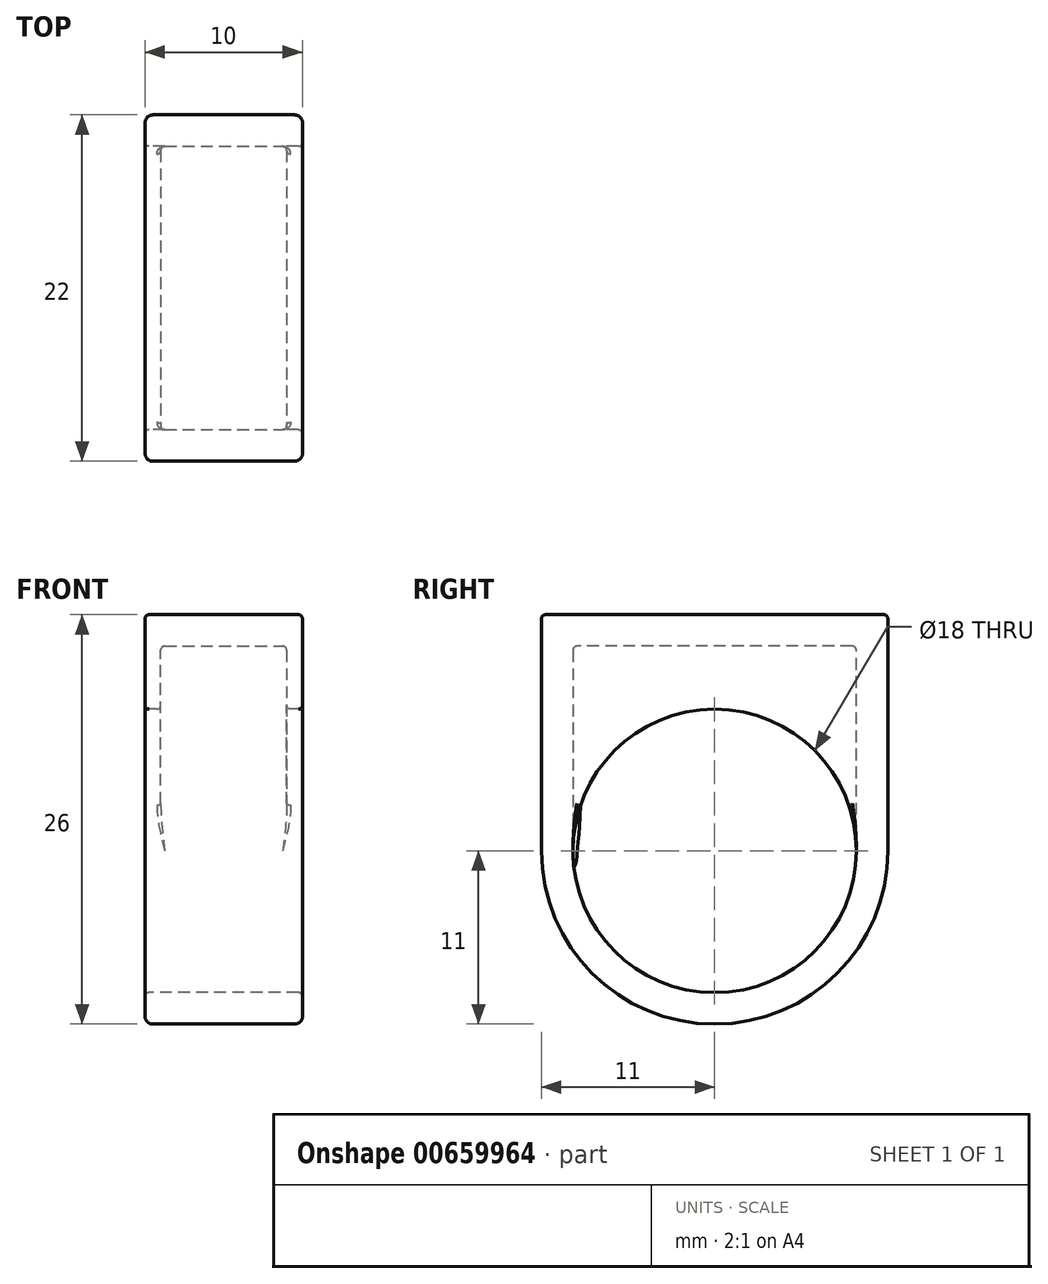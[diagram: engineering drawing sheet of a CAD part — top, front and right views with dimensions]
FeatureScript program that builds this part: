
annotation { "Feature Type Name" : "Feature", "Feature Type Description" : "" }
export const myFeature = defineFeature(function(context is Context, id is Id, definition is map)
    precondition{}
    {
        {
            var Q0;
            Q0=qCreatedBy(makeId("Right.planeOp"),FACE);
            var sketch = newSketch(context, id + "F0", { "sketchPlane" : qUnion([Q0])});
            skCircle(sketch, "E0", {"center": v(0, 0) * mm, "radius": 9 * mm});
            skCircle(sketch, "E1", {"center": v(0, 0) * mm, "radius": 11 * mm});
            skLineSegment(sketch, "E2", {"start": v(-11, 0) * mm, "end": v(-11, 15) * mm});
            skLineSegment(sketch, "E3", {"start": v(11, 0) * mm, "end": v(11, 15) * mm});
            skLineSegment(sketch, "E4", {"start": v(-11, 15) * mm, "end": v(11, 15) * mm});
            skSolve(sketch);
        }
        {
            var Q0;
            Q0=qSketchRegion(id+"F0",true);
            extrude(context, id + "F1", {"entities" : qUnion([Q0]), "endBound" : BoundingType.SYMMETRIC, "depth" : 10 * mm, "offsetDistance" : 25 * mm});
        }
        {
            var Q0;
            Q0=qCreatedBy(makeId("Right.planeOp"),FACE);
            var sketch = newSketch(context, id + "F2", { "sketchPlane" : qUnion([Q0])});
            skLineSegment(sketch, "E5.0", {"start": v(-9, 13) * mm, "end": v(-9, 0) * mm});
            skLineSegment(sketch, "E5.1", {"start": v(9, 13) * mm, "end": v(-9, 13) * mm});
            skLineSegment(sketch, "E5.2", {"start": v(9, 0) * mm, "end": v(9, 13) * mm});
            skArc(sketch, "E5.3", {"start": v(-9, 0) * mm, "mid": v(0, -9) * mm, "end": v(9, 0) * mm});
            skSolve(sketch);
        }
        {
            var Q0;
            Q0 = qSketchRegion(id + "F2", true);
            extrude(context, id + "F3", {"entities" : qUnion([Q0]), "operationType" : NewBodyOperationType.REMOVE, "endBound" : BoundingType.SYMMETRIC, "oppositeDirection" : true, "depth" : 8 * mm, "offsetDistance" : 25 * mm});
        }
        {
            var Q0;
            Q0=makeQuery(id+"F1.opExtrude","CAP_EDGE",EDGE,{"disambiguationData":[OSD([sQuery(id+"F0.wireOp",EDGE,"E2")])],"isStart":false});
            var Q1;
            Q1=makeQuery(id+"F1.opExtrude","CAP_EDGE",EDGE,{"disambiguationData":[OSD([sQuery(id+"F0.wireOp",EDGE,"E2")])],"isStart":true});
            fillet(context, id + "F4", {"entities" : qUnion([Q0, Q1]), "radius" : 0.5 * mm, "tangentPropagation" : true, "allowEdgeOverflow" : false});
        }
        {
            var Q0;
            {var subQ0=sQuery(id+"F0.wireOp",EDGE,"E2");Q0=makeQuery(id+"F4.opFillet","BLEND_EDGE",EDGE,{"blendedFrom":[makeQuery(id+"F1.opExtrude","CAP_EDGE",EDGE,{"disambiguationData":[OSD([subQ0])],"isStart":true}),makeQuery(id+"F1.opExtrude","SWEPT_FACE",FACE,{"disambiguationData":[OSD([subQ0])]})],"blendedInto":[makeQuery(id+"F1.opExtrude","SWEPT_FACE",FACE,{"disambiguationData":[OSD([subQ0])]})]});}
            var Q1;
            {var subQ0=sQuery(id+"F0.wireOp",EDGE,"E2");Q1=makeQuery(id+"F4.opFillet","BLEND_EDGE",EDGE,{"blendedFrom":[makeQuery(id+"F1.opExtrude","CAP_EDGE",EDGE,{"disambiguationData":[OSD([subQ0])],"isStart":false}),makeQuery(id+"F1.opExtrude","SWEPT_FACE",FACE,{"disambiguationData":[OSD([subQ0])]})],"blendedInto":[makeQuery(id+"F1.opExtrude","SWEPT_FACE",FACE,{"disambiguationData":[OSD([subQ0])]})]});}
            var Q2;
            Q2=makeQuery(id+"F1.opExtrude","CAP_EDGE",EDGE,{"disambiguationData":[OSD([sQuery(id+"F0.wireOp",EDGE,"E0")])],"isStart":false});
            var Q3;
            Q3=makeQuery(id+"F4.opFillet","BLEND_EDGE",EDGE,{"blendedFrom":[makeQuery(id+"F1.opExtrude","CAP_EDGE",EDGE,{"disambiguationData":[OSD([sQuery(id+"F0.wireOp",EDGE,"E1")])],"isStart":false}),makeQuery(id+"F1.opExtrude","CAP_EDGE",EDGE,{"disambiguationData":[OSD([sQuery(id+"F0.wireOp",EDGE,"E3")])],"isStart":false})],"blendedInto":[]});
            var Q4;
            Q4=makeQuery(id+"F1.opExtrude","SWEPT_EDGE",EDGE,{"disambiguationData":[OSD([sQuery(id+"F0.wireOp",EDGE,"E3"),sQuery(id+"F0.wireOp",EDGE,"E4")])]});
            var Q5;
            Q5=makeQuery(id+"F1.opExtrude","SWEPT_EDGE",EDGE,{"disambiguationData":[OSD([sQuery(id+"F0.wireOp",EDGE,"E1"),sQuery(id+"F0.wireOp",EDGE,"E3")])]});
            var Q6;
            {var subQ0=sQuery(id+"F0.wireOp",EDGE,"E2");Q6=makeQuery(id+"F4.opFillet","BLEND_EDGE",EDGE,{"blendedFrom":[makeQuery(id+"F1.opExtrude","CAP_EDGE",EDGE,{"disambiguationData":[OSD([subQ0])],"isStart":false}),makeQuery(id+"F1.opExtrude","CAP_FACE",FACE,{"disambiguationData":[OSD([sQuery(id+"F0.wireOp",EDGE,"E0"),sQuery(id+"F0.wireOp",EDGE,"E1"),subQ0,sQuery(id+"F0.wireOp",EDGE,"E3"),sQuery(id+"F0.wireOp",EDGE,"E4")])],"isStart":false})],"blendedInto":[makeQuery(id+"F1.opExtrude","CAP_FACE",FACE,{"disambiguationData":[OSD([sQuery(id+"F0.wireOp",EDGE,"E0"),sQuery(id+"F0.wireOp",EDGE,"E1"),subQ0,sQuery(id+"F0.wireOp",EDGE,"E3"),sQuery(id+"F0.wireOp",EDGE,"E4")])],"isStart":false})]});}
            var Q7;
            Q7=makeQuery(id+"F4.opFillet","BLEND_EDGE",EDGE,{"blendedFrom":[makeQuery(id+"F1.opExtrude","CAP_EDGE",EDGE,{"disambiguationData":[OSD([sQuery(id+"F0.wireOp",EDGE,"E3")])],"isStart":false}),makeQuery(id+"F1.opExtrude","SWEPT_FACE",FACE,{"disambiguationData":[OSD([sQuery(id+"F0.wireOp",EDGE,"E4")])]})],"blendedInto":[makeQuery(id+"F1.opExtrude","SWEPT_FACE",FACE,{"disambiguationData":[OSD([sQuery(id+"F0.wireOp",EDGE,"E4")])]})]});
            var Q8;
            Q8=makeQuery(id+"F3.boolean.opBoolean","INTERSECT",EDGE,{"derivedFrom":[makeQuery(id+"F1.opExtrude","SWEPT_FACE",FACE,{"disambiguationData":[OSD([sQuery(id+"F0.wireOp",EDGE,"E0")])]}),makeQuery(id+"F3.opExtrude","CAP_FACE",FACE,{"disambiguationData":[OSD([sQuery(id+"F2.wireOp",EDGE,"E5.0"),sQuery(id+"F2.wireOp",EDGE,"E5.1"),sQuery(id+"F2.wireOp",EDGE,"E5.2"),sQuery(id+"F2.wireOp",EDGE,"E5.3")])],"isStart":false})]});
            var Q9;
            Q9=makeQuery(id+"F3.boolean.opBoolean","INTERSECT",EDGE,{"derivedFrom":[makeQuery(id+"F1.opExtrude","SWEPT_FACE",FACE,{"disambiguationData":[OSD([sQuery(id+"F0.wireOp",EDGE,"E0")])]}),makeQuery(id+"F3.opExtrude","CAP_FACE",FACE,{"disambiguationData":[OSD([sQuery(id+"F2.wireOp",EDGE,"E5.0"),sQuery(id+"F2.wireOp",EDGE,"E5.1"),sQuery(id+"F2.wireOp",EDGE,"E5.2"),sQuery(id+"F2.wireOp",EDGE,"E5.3")])],"isStart":true})]});
            var Q10;
            Q10=makeQuery(id+"F1.opExtrude","CAP_EDGE",EDGE,{"disambiguationData":[OSD([sQuery(id+"F0.wireOp",EDGE,"E0")])],"isStart":true});
            var Q11;
            {var subQ0=sQuery(id+"F0.wireOp",EDGE,"E1");Q11=makeQuery(id+"F4.opFillet","BLEND_EDGE",EDGE,{"blendedFrom":[makeQuery(id+"F1.opExtrude","CAP_EDGE",EDGE,{"disambiguationData":[OSD([subQ0])],"isStart":true}),makeQuery(id+"F1.opExtrude","SWEPT_FACE",FACE,{"disambiguationData":[OSD([subQ0])]})],"blendedInto":[makeQuery(id+"F1.opExtrude","SWEPT_FACE",FACE,{"disambiguationData":[OSD([subQ0])]})]});}
            var Q12;
            {var subQ0=sQuery(id+"F0.wireOp",EDGE,"E3");Q12=makeQuery(id+"F4.opFillet","BLEND_EDGE",EDGE,{"blendedFrom":[makeQuery(id+"F1.opExtrude","CAP_EDGE",EDGE,{"disambiguationData":[OSD([subQ0])],"isStart":false}),makeQuery(id+"F1.opExtrude","SWEPT_FACE",FACE,{"disambiguationData":[OSD([subQ0])]})],"blendedInto":[makeQuery(id+"F1.opExtrude","SWEPT_FACE",FACE,{"disambiguationData":[OSD([subQ0])]})]});}
            var Q13;
            {var subQ0=sQuery(id+"F0.wireOp",EDGE,"E2");Q13=makeQuery(id+"F4.opFillet","BLEND_EDGE",EDGE,{"blendedFrom":[makeQuery(id+"F1.opExtrude","CAP_EDGE",EDGE,{"disambiguationData":[OSD([subQ0])],"isStart":true}),makeQuery(id+"F1.opExtrude","CAP_FACE",FACE,{"disambiguationData":[OSD([sQuery(id+"F0.wireOp",EDGE,"E0"),sQuery(id+"F0.wireOp",EDGE,"E1"),subQ0,sQuery(id+"F0.wireOp",EDGE,"E3"),sQuery(id+"F0.wireOp",EDGE,"E4")])],"isStart":true})],"blendedInto":[makeQuery(id+"F1.opExtrude","CAP_FACE",FACE,{"disambiguationData":[OSD([sQuery(id+"F0.wireOp",EDGE,"E0"),sQuery(id+"F0.wireOp",EDGE,"E1"),subQ0,sQuery(id+"F0.wireOp",EDGE,"E3"),sQuery(id+"F0.wireOp",EDGE,"E4")])],"isStart":true})]});}
            var Q14;
            {var subQ0=sQuery(id+"F0.wireOp",EDGE,"E1");Q14=makeQuery(id+"F4.opFillet","BLEND_EDGE",EDGE,{"blendedFrom":[makeQuery(id+"F1.opExtrude","CAP_EDGE",EDGE,{"disambiguationData":[OSD([subQ0])],"isStart":false}),makeQuery(id+"F1.opExtrude","SWEPT_FACE",FACE,{"disambiguationData":[OSD([subQ0])]})],"blendedInto":[makeQuery(id+"F1.opExtrude","SWEPT_FACE",FACE,{"disambiguationData":[OSD([subQ0])]})]});}
            var Q15;
            {var subQ0=sQuery(id+"F0.wireOp",EDGE,"E1");Q15=makeQuery(id+"F4.opFillet","BLEND_EDGE",EDGE,{"blendedFrom":[makeQuery(id+"F1.opExtrude","CAP_EDGE",EDGE,{"disambiguationData":[OSD([subQ0])],"isStart":false}),makeQuery(id+"F1.opExtrude","CAP_FACE",FACE,{"disambiguationData":[OSD([sQuery(id+"F0.wireOp",EDGE,"E0"),subQ0,sQuery(id+"F0.wireOp",EDGE,"E2"),sQuery(id+"F0.wireOp",EDGE,"E3"),sQuery(id+"F0.wireOp",EDGE,"E4")])],"isStart":false})],"blendedInto":[makeQuery(id+"F1.opExtrude","CAP_FACE",FACE,{"disambiguationData":[OSD([sQuery(id+"F0.wireOp",EDGE,"E0"),subQ0,sQuery(id+"F0.wireOp",EDGE,"E2"),sQuery(id+"F0.wireOp",EDGE,"E3"),sQuery(id+"F0.wireOp",EDGE,"E4")])],"isStart":false})]});}
            var Q16;
            {var subQ0=sQuery(id+"F0.wireOp",EDGE,"E1");Q16=makeQuery(id+"F4.opFillet","BLEND_EDGE",EDGE,{"blendedFrom":[makeQuery(id+"F1.opExtrude","CAP_EDGE",EDGE,{"disambiguationData":[OSD([subQ0])],"isStart":true}),makeQuery(id+"F1.opExtrude","CAP_FACE",FACE,{"disambiguationData":[OSD([sQuery(id+"F0.wireOp",EDGE,"E0"),subQ0,sQuery(id+"F0.wireOp",EDGE,"E2"),sQuery(id+"F0.wireOp",EDGE,"E3"),sQuery(id+"F0.wireOp",EDGE,"E4")])],"isStart":true})],"blendedInto":[makeQuery(id+"F1.opExtrude","CAP_FACE",FACE,{"disambiguationData":[OSD([sQuery(id+"F0.wireOp",EDGE,"E0"),subQ0,sQuery(id+"F0.wireOp",EDGE,"E2"),sQuery(id+"F0.wireOp",EDGE,"E3"),sQuery(id+"F0.wireOp",EDGE,"E4")])],"isStart":true})]});}
            var Q17;
            Q17=makeQuery(id+"F3.boolean.opBoolean","COPY",EDGE,{"derivedFrom":makeQuery(id+"F3.opExtrude","CAP_EDGE",EDGE,{"disambiguationData":[OSD([sQuery(id+"F2.wireOp",EDGE,"E5.1")])],"isStart":true})});
            var Q18;
            Q18=makeQuery(id+"F3.boolean.opBoolean","COPY",EDGE,{"derivedFrom":makeQuery(id+"F3.opExtrude","SWEPT_EDGE",EDGE,{"disambiguationData":[OSD([sQuery(id+"F2.wireOp",EDGE,"E5.0"),sQuery(id+"F2.wireOp",EDGE,"E5.3")])]})});
            var Q19;
            Q19=makeQuery(id+"F3.boolean.opBoolean","COPY",EDGE,{"derivedFrom":makeQuery(id+"F3.opExtrude","SWEPT_EDGE",EDGE,{"disambiguationData":[OSD([sQuery(id+"F2.wireOp",EDGE,"E5.2"),sQuery(id+"F2.wireOp",EDGE,"E5.3")])]})});
            var Q20;
            Q20=makeQuery(id+"F1.opExtrude","CAP_EDGE",EDGE,{"disambiguationData":[OSD([sQuery(id+"F0.wireOp",EDGE,"E4")])],"isStart":false});
            var Q21;
            Q21=makeQuery(id+"F3.boolean.opBoolean","COPY",EDGE,{"derivedFrom":makeQuery(id+"F3.opExtrude","SWEPT_EDGE",EDGE,{"disambiguationData":[OSD([sQuery(id+"F2.wireOp",EDGE,"E5.1"),sQuery(id+"F2.wireOp",EDGE,"E5.2")])]})});
            var Q22;
            Q22=makeQuery(id+"F3.boolean.opBoolean","COPY",EDGE,{"derivedFrom":makeQuery(id+"F3.opExtrude","SWEPT_EDGE",EDGE,{"disambiguationData":[OSD([sQuery(id+"F2.wireOp",EDGE,"E5.0"),sQuery(id+"F2.wireOp",EDGE,"E5.1")])]})});
            var Q23;
            {var subQ0=sQuery(id+"F0.wireOp",EDGE,"E3");Q23=makeQuery(id+"F4.opFillet","BLEND_EDGE",EDGE,{"blendedFrom":[makeQuery(id+"F1.opExtrude","CAP_EDGE",EDGE,{"disambiguationData":[OSD([subQ0])],"isStart":false}),makeQuery(id+"F1.opExtrude","CAP_FACE",FACE,{"disambiguationData":[OSD([sQuery(id+"F0.wireOp",EDGE,"E0"),sQuery(id+"F0.wireOp",EDGE,"E1"),sQuery(id+"F0.wireOp",EDGE,"E2"),subQ0,sQuery(id+"F0.wireOp",EDGE,"E4")])],"isStart":false})],"blendedInto":[makeQuery(id+"F1.opExtrude","CAP_FACE",FACE,{"disambiguationData":[OSD([sQuery(id+"F0.wireOp",EDGE,"E0"),sQuery(id+"F0.wireOp",EDGE,"E1"),sQuery(id+"F0.wireOp",EDGE,"E2"),subQ0,sQuery(id+"F0.wireOp",EDGE,"E4")])],"isStart":false})]});}
            var Q24;
            Q24=makeQuery(id+"F1.opExtrude","CAP_EDGE",EDGE,{"disambiguationData":[OSD([sQuery(id+"F0.wireOp",EDGE,"E4")])],"isStart":true});
            var Q25;
            Q25=makeQuery(id+"F3.boolean.opBoolean","COPY",EDGE,{"derivedFrom":makeQuery(id+"F3.opExtrude","CAP_EDGE",EDGE,{"disambiguationData":[OSD([sQuery(id+"F2.wireOp",EDGE,"E5.1")])],"isStart":false})});
            var Q26;
            Q26=makeQuery(id+"F1.opExtrude","SWEPT_EDGE",EDGE,{"disambiguationData":[OSD([sQuery(id+"F0.wireOp",EDGE,"E2"),sQuery(id+"F0.wireOp",EDGE,"E4")])]});
            var Q27;
            Q27=makeQuery(id+"F4.opFillet","BLEND_EDGE",EDGE,{"blendedFrom":[makeQuery(id+"F1.opExtrude","CAP_EDGE",EDGE,{"disambiguationData":[OSD([sQuery(id+"F0.wireOp",EDGE,"E1")])],"isStart":false}),makeQuery(id+"F1.opExtrude","CAP_EDGE",EDGE,{"disambiguationData":[OSD([sQuery(id+"F0.wireOp",EDGE,"E2")])],"isStart":false})],"blendedInto":[]});
            var Q28;
            Q28=makeQuery(id+"F3.boolean.opBoolean","COPY",EDGE,{"derivedFrom":makeQuery(id+"F3.opExtrude","CAP_EDGE",EDGE,{"disambiguationData":[OSD([sQuery(id+"F2.wireOp",EDGE,"E5.2")])],"isStart":true})});
            var Q29;
            Q29=makeQuery(id+"F4.opFillet","BLEND_EDGE",EDGE,{"blendedFrom":[makeQuery(id+"F1.opExtrude","CAP_EDGE",EDGE,{"disambiguationData":[OSD([sQuery(id+"F0.wireOp",EDGE,"E2")])],"isStart":false}),makeQuery(id+"F1.opExtrude","SWEPT_FACE",FACE,{"disambiguationData":[OSD([sQuery(id+"F0.wireOp",EDGE,"E4")])]})],"blendedInto":[makeQuery(id+"F1.opExtrude","SWEPT_FACE",FACE,{"disambiguationData":[OSD([sQuery(id+"F0.wireOp",EDGE,"E4")])]})]});
            var Q30;
            {var subQ0=sQuery(id+"F0.wireOp",EDGE,"E3");Q30=makeQuery(id+"F4.opFillet","BLEND_EDGE",EDGE,{"blendedFrom":[makeQuery(id+"F1.opExtrude","CAP_EDGE",EDGE,{"disambiguationData":[OSD([subQ0])],"isStart":true}),makeQuery(id+"F1.opExtrude","CAP_FACE",FACE,{"disambiguationData":[OSD([sQuery(id+"F0.wireOp",EDGE,"E0"),sQuery(id+"F0.wireOp",EDGE,"E1"),sQuery(id+"F0.wireOp",EDGE,"E2"),subQ0,sQuery(id+"F0.wireOp",EDGE,"E4")])],"isStart":true})],"blendedInto":[makeQuery(id+"F1.opExtrude","CAP_FACE",FACE,{"disambiguationData":[OSD([sQuery(id+"F0.wireOp",EDGE,"E0"),sQuery(id+"F0.wireOp",EDGE,"E1"),sQuery(id+"F0.wireOp",EDGE,"E2"),subQ0,sQuery(id+"F0.wireOp",EDGE,"E4")])],"isStart":true})]});}
            var Q31;
            Q31=makeQuery(id+"F4.opFillet","BLEND_EDGE",EDGE,{"blendedFrom":[makeQuery(id+"F1.opExtrude","CAP_EDGE",EDGE,{"disambiguationData":[OSD([sQuery(id+"F0.wireOp",EDGE,"E1")])],"isStart":true}),makeQuery(id+"F1.opExtrude","CAP_EDGE",EDGE,{"disambiguationData":[OSD([sQuery(id+"F0.wireOp",EDGE,"E3")])],"isStart":true})],"blendedInto":[]});
            var Q32;
            Q32=makeQuery(id+"F1.opExtrude","SWEPT_EDGE",EDGE,{"disambiguationData":[OSD([sQuery(id+"F0.wireOp",EDGE,"E1"),sQuery(id+"F0.wireOp",EDGE,"E2")])]});
            var Q33;
            Q33=makeQuery(id+"F4.opFillet","BLEND_EDGE",EDGE,{"blendedFrom":[makeQuery(id+"F1.opExtrude","CAP_EDGE",EDGE,{"disambiguationData":[OSD([sQuery(id+"F0.wireOp",EDGE,"E2")])],"isStart":true}),makeQuery(id+"F1.opExtrude","SWEPT_FACE",FACE,{"disambiguationData":[OSD([sQuery(id+"F0.wireOp",EDGE,"E4")])]})],"blendedInto":[makeQuery(id+"F1.opExtrude","SWEPT_FACE",FACE,{"disambiguationData":[OSD([sQuery(id+"F0.wireOp",EDGE,"E4")])]})]});
            var Q34;
            Q34=makeQuery(id+"F3.boolean.opBoolean","COPY",EDGE,{"derivedFrom":makeQuery(id+"F3.opExtrude","CAP_EDGE",EDGE,{"disambiguationData":[OSD([sQuery(id+"F2.wireOp",EDGE,"E5.2")])],"isStart":false})});
            var Q35;
            Q35=makeQuery(id+"F3.boolean.opBoolean","COPY",EDGE,{"derivedFrom":makeQuery(id+"F3.opExtrude","CAP_EDGE",EDGE,{"disambiguationData":[OSD([sQuery(id+"F2.wireOp",EDGE,"E5.0")])],"isStart":true})});
            var Q36;
            {var subQ0=sQuery(id+"F0.wireOp",EDGE,"E3");Q36=makeQuery(id+"F4.opFillet","BLEND_EDGE",EDGE,{"blendedFrom":[makeQuery(id+"F1.opExtrude","CAP_EDGE",EDGE,{"disambiguationData":[OSD([subQ0])],"isStart":true}),makeQuery(id+"F1.opExtrude","SWEPT_FACE",FACE,{"disambiguationData":[OSD([subQ0])]})],"blendedInto":[makeQuery(id+"F1.opExtrude","SWEPT_FACE",FACE,{"disambiguationData":[OSD([subQ0])]})]});}
            var Q37;
            Q37=makeQuery(id+"F4.opFillet","BLEND_EDGE",EDGE,{"blendedFrom":[makeQuery(id+"F1.opExtrude","CAP_EDGE",EDGE,{"disambiguationData":[OSD([sQuery(id+"F0.wireOp",EDGE,"E3")])],"isStart":true}),makeQuery(id+"F1.opExtrude","SWEPT_FACE",FACE,{"disambiguationData":[OSD([sQuery(id+"F0.wireOp",EDGE,"E4")])]})],"blendedInto":[makeQuery(id+"F1.opExtrude","SWEPT_FACE",FACE,{"disambiguationData":[OSD([sQuery(id+"F0.wireOp",EDGE,"E4")])]})]});
            var Q38;
            Q38=makeQuery(id+"F3.boolean.opBoolean","COPY",EDGE,{"derivedFrom":makeQuery(id+"F3.opExtrude","CAP_EDGE",EDGE,{"disambiguationData":[OSD([sQuery(id+"F2.wireOp",EDGE,"E5.0")])],"isStart":false})});
            var Q39;
            Q39=makeQuery(id+"F4.opFillet","BLEND_EDGE",EDGE,{"blendedFrom":[makeQuery(id+"F1.opExtrude","CAP_EDGE",EDGE,{"disambiguationData":[OSD([sQuery(id+"F0.wireOp",EDGE,"E1")])],"isStart":true}),makeQuery(id+"F1.opExtrude","CAP_EDGE",EDGE,{"disambiguationData":[OSD([sQuery(id+"F0.wireOp",EDGE,"E2")])],"isStart":true})],"blendedInto":[]});
            fillet(context, id + "F5", {"entities" : qUnion([Q0, Q1, Q2, Q3, Q4, Q5, Q6, Q7, Q8, Q9, Q10, Q11, Q12, Q13, Q14, Q15, Q16, Q17, Q18, Q19, Q20, Q21, Q22, Q23, Q24, Q25, Q26, Q27, Q28, Q29, Q30, Q31, Q32, Q33, Q34, Q35, Q36, Q37, Q38, Q39]), "radius" : 0.25 * mm, "tangentPropagation" : true, "allowEdgeOverflow" : false});
        }
    });
